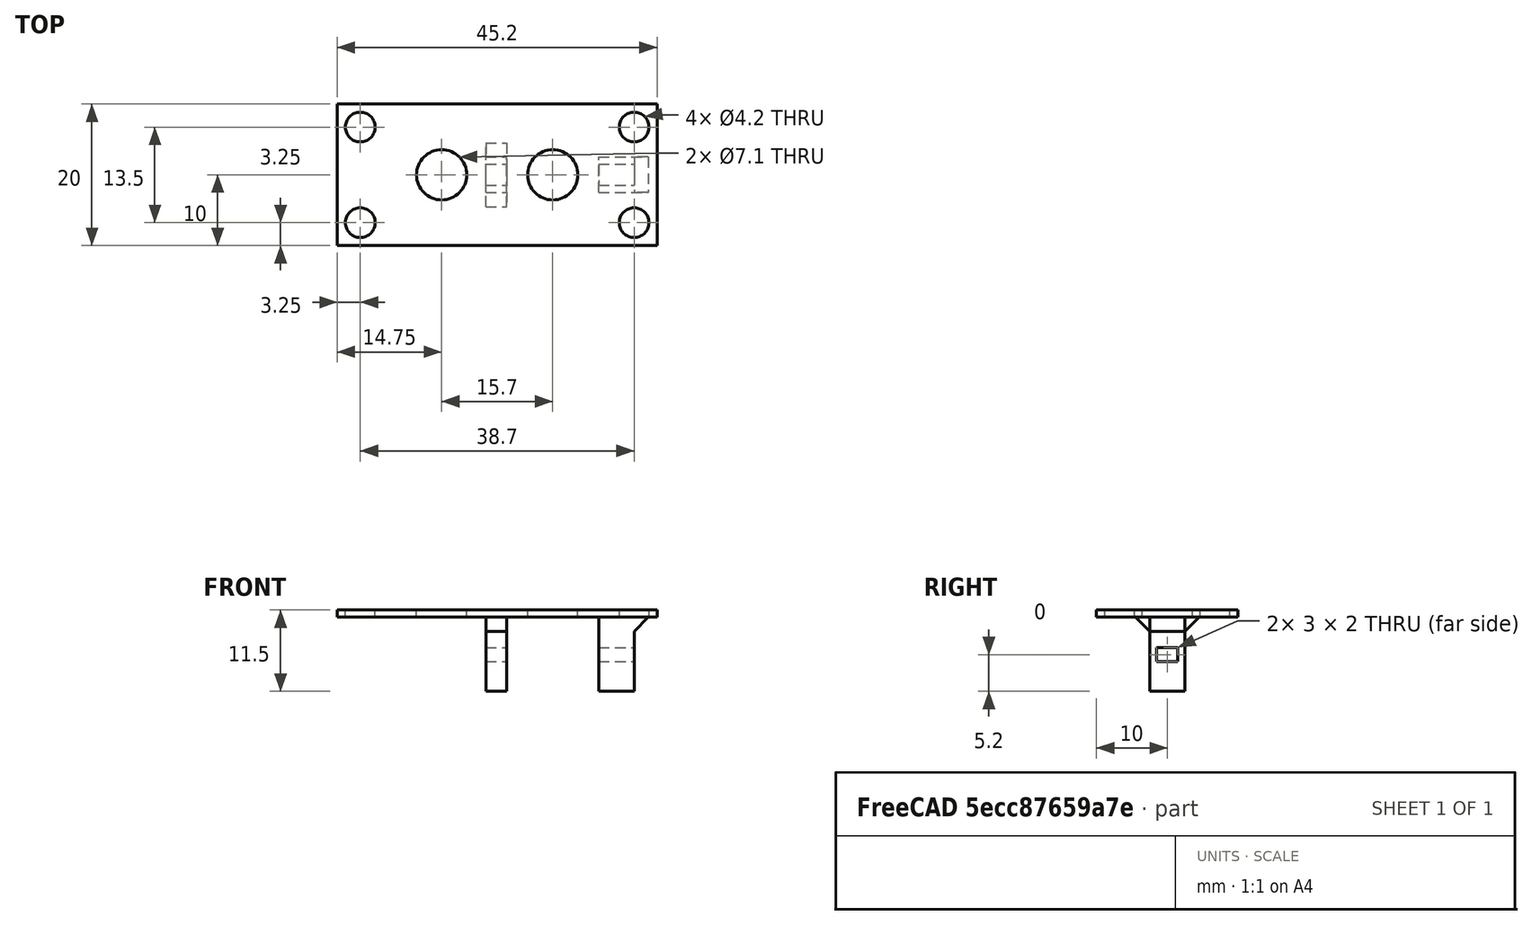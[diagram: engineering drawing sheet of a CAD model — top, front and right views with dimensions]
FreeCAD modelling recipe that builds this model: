
FCSTD DOCUMENT  (FreeCAD 0.17R13522 (Git))
Label: v5_base2_media_con_soportes
License: CreativeCommons Attribution-ShareAlike
LicenseURL: http://creativecommons.org/licenses/by-sa/4.0/
objects: Part::Cut×17, Part::Box×10, Part::Cylinder×8, Part::Feature×6, Part::Fuse×6, Part::Chamfer×4
note: 51 computed .brp shape members not serialized (recipe doc carries the construction recipe); baked Part::Feature solids carry a one-line shape summary decoded from their .brp

FEATURE [Part::Box] Box  label="base"
  AttacherType = Attacher::AttachEngine3D
  Height = 2
  Length = 45.2
  Width = 20
FEATURE [Part::Cylinder] Cylinder  label="cortador izquierda"
  Angle = 360
  AttacherType = Attacher::AttachEngine3D
  Height = 60
  Placement = pos=(14.75,10,-12) rot=(0,0,1;0rad)
  Radius = 3.55
FEATURE [Part::Feature] Cylinder001  label="cortador derecha"
  Placement = pos=(30.45,10,-4) rot=(0,0,1;0rad)
  shape: bbox 7.1 x 7.1 x 10 mm, 3 faces (baked)
FEATURE [Part::Cylinder] Cylinder002  label="sacabocado_abajo_izq"
  Angle = 360
  AttacherType = Attacher::AttachEngine3D
  Height = 10
  Placement = pos=(3,3,-4) rot=(0,0,1;0rad)
  Radius = 1.75
FEATURE [Part::Feature] Cylinder002001  label="sacabocado_abajo_derecha"
  Placement = pos=(42.2,3,-4) rot=(0,0,1;0rad)
  shape: bbox 3.5 x 3.5 x 10 mm, 3 faces (baked)
FEATURE [Part::Feature] Cylinder002002  label="sacabocado_arriba_izq"
  Placement = pos=(3,17,-4) rot=(0,0,1;0rad)
  shape: bbox 3.5 x 3.5 x 10 mm, 3 faces (baked)
FEATURE [Part::Feature] Cylinder002002001  label="sacabocado_arriba_derecha"
  Placement = pos=(42.2,17,-4) rot=(0,0,1;0rad)
  shape: bbox 3.5 x 3.5 x 10 mm, 3 faces (baked)
FEATURE [Part::Cylinder] Cylinder002002002  label="cilindro interior"
  Angle = 360
  AttacherType = Attacher::AttachEngine3D
  Height = 38.5
  Placement = pos=(14.75,10,0) rot=(0,0,1;0rad)
  Radius = 4.5
FEATURE [Part::Cylinder] Cylinder002002003  label="base cilindrica grande"
  Angle = 360
  AttacherType = Attacher::AttachEngine3D
  Height = 8.5
  Placement = pos=(14.75,10,0) rot=(0,0,1;0rad)
  Radius = 7
FEATURE [Part::Cut] Cut
  Base = -> Box
  Refine = true
  Tool = -> Cylinder002
FEATURE [Part::Cut] Cut001
  Base = -> Cut
  Refine = true
  Tool = -> Cylinder002001
FEATURE [Part::Cut] Cut002
  Base = -> Cut001
  Refine = true
  Tool = -> Cylinder001
FEATURE [Part::Cut] Cut003
  Base = -> Cut002
  Refine = true
  Tool = -> Cylinder002002001
FEATURE [Part::Cut] Cut004
  Base = -> Cut003
  Refine = true
  Tool = -> Cylinder002002
FEATURE [Part::Fuse] Fusion
  Base = -> Cylinder002002003
  Refine = true
  Tool = -> Cut004
FEATURE [Part::Fuse] Fusion001
  Base = -> Cylinder002002002
  Refine = true
  Tool = -> Fusion
FEATURE [Part::Cut] Cut005  label="pieza sin soportes"
  Base = -> Fusion001
  Refine = true
  Tool = -> Cylinder
FEATURE [Part::Box] Box001  label="soporte1"
  AttacherType = Attacher::AttachEngine3D
  Height = 10.5
  Length = 5
  Placement = pos=(36.95,7.5,-10.5) rot=(0,0,1;0rad)
  Width = 5
FEATURE [Part::Feature] Box001001  label="soporte2"
  Placement = pos=(18.95,7.5,-10.5) rot=(0,0,1;0rad)
  shape: bbox 5 x 5 x 10.5 mm, 6 faces (baked)
FEATURE [Part::Box] Box001002  label="perforador chavetas"
  AttacherType = Attacher::AttachEngine3D
  Height = 2
  Length = 30
  Placement = pos=(16,8.5,-6.3) rot=(0,0,1;0rad)
  Width = 3
FEATURE [Part::Feature] Box001002001  label="perforador chavetas001"
  Placement = pos=(16,8.5,-6.3) rot=(0,0,1;0rad)
  shape: bbox 30 x 3 x 2 mm, 6 faces (baked)
FEATURE [Part::Cut] Cut006
  Base = -> Box001
  Refine = true
  Tool = -> Box001002
FEATURE [Part::Cut] Cut007
  Base = -> Box001001
  Refine = true
  Tool = -> Box001002001
FEATURE [Part::Fuse] Fusion002
  Base = -> Cut005
  Refine = true
  Tool = -> Cut007
FEATURE [Part::Fuse] Fusion003
  Base = -> Cut006
  Refine = true
  Tool = -> Fusion002
FEATURE [Part::Chamfer] Chamfer
  Base = -> Fusion003
  Edges = 1 edges r=2: [Edge29]
FEATURE [Part::Chamfer] Chamfer001
  Base = -> Chamfer
  Edges = 1 edges r=2: [Edge19]
FEATURE [Part::Chamfer] Chamfer002  label="pieza completa"
  Base = -> Chamfer001
  Edges = 2 edges r=2: [Edge4,Edge10]
FEATURE [Part::Box] Box001002002  label="cortador separa pieza 2"
  AttacherType = Attacher::AttachEngine3D
  Height = 26
  Length = 58
  Placement = pos=(-10.65,-6,1) rot=(0,0,1;0rad)
  Width = 30
FEATURE [Part::Box] Box001002004  label="Cube"
  AttacherType = Attacher::AttachEngine3D
  Height = 30
  Length = 30
  Placement = pos=(0,0,18) rot=(0,0,1;0rad)
  Width = 30
FEATURE [Part::Cut] Cut008
  Base = -> Chamfer002
  Refine = true
  Tool = -> Box001002004
FEATURE [Part::Cut] Cut009
  Base = -> Cut008
  Refine = true
  Tool = -> Box001002002
FEATURE [Part::Cylinder] Cylinder002002004  label="Cylinder"
  Angle = 360
  AttacherType = Attacher::AttachEngine3D
  Height = 10
  Placement = pos=(41.95,16.75,-4) rot=(0,0,1;0rad)
  Radius = 2.1
FEATURE [Part::Cylinder] Cylinder002002005  label="Cylinder001"
  Angle = 360
  AttacherType = Attacher::AttachEngine3D
  Height = 10
  Placement = pos=(41.95,3.25,-3.5) rot=(0,0,1;0rad)
  Radius = 2.1
FEATURE [Part::Cylinder] Cylinder002002006  label="Cylinder002"
  Angle = 360
  AttacherType = Attacher::AttachEngine3D
  Height = 10
  Placement = pos=(3.25,16.75,-4) rot=(0,0,1;0rad)
  Radius = 2.1
FEATURE [Part::Cylinder] Cylinder002002007  label="Cylinder003"
  Angle = 360
  AttacherType = Attacher::AttachEngine3D
  Height = 10
  Placement = pos=(3.25,3.25,-4) rot=(0,0,1;0rad)
  Radius = 2.1
FEATURE [Part::Box] Box001002005  label="Cube001"
  AttacherType = Attacher::AttachEngine3D
  Height = 1
  Length = 10
  Width = 20
FEATURE [Part::Fuse] Fusion004
  Base = -> Cut009
  Refine = true
  Tool = -> Box001002005
FEATURE [Part::Cut] Cut010
  Base = -> Fusion004
  Refine = true
  Tool = -> Cylinder002002007
FEATURE [Part::Cut] Cut011
  Base = -> Cut010
  Refine = true
  Tool = -> Cylinder002002006
FEATURE [Part::Box] Box001002006  label="Cube002"
  AttacherType = Attacher::AttachEngine3D
  Height = 1
  Length = 10
  Placement = pos=(35,0,0) rot=(0,0,1;0rad)
  Width = 20
FEATURE [Part::Fuse] Fusion005
  Base = -> Cut011
  Refine = true
  Tool = -> Box001002006
FEATURE [Part::Cut] Cut012
  Base = -> Fusion005
  Refine = true
  Tool = -> Cylinder002002004
FEATURE [Part::Cut] Cut013
  Base = -> Cut012
  Refine = true
  Tool = -> Cylinder002002005
FEATURE [Part::Box] Box001002007  label="Cube003"
  AttacherType = Attacher::AttachEngine3D
  Height = 6
  Length = 6
  Placement = pos=(36,12.5,-6) rot=(0,0,1;0rad)
  Width = 2
FEATURE [Part::Cut] Cut014
  Base = -> Cut013
  Refine = true
  Tool = -> Box001002007
FEATURE [Part::Box] Box001002008  label="Cube004"
  AttacherType = Attacher::AttachEngine3D
  Height = 10
  Length = 6
  Placement = pos=(36.5,5.5,-10) rot=(0,0,1;0rad)
  Width = 2
FEATURE [Part::Cut] Cut015
  Base = -> Cut014
  Refine = true
  Tool = -> Box001002008
FEATURE [Part::Chamfer] Chamfer003
  Base = -> Cut015
  Edges = 1 edges r=2: [Edge38]
FEATURE [Part::Box] Box001002009  label="Cube005"
  AttacherType = Attacher::AttachEngine3D
  Height = 18
  Length = 10
  Placement = pos=(11,0,-18) rot=(0,0,1;0rad)
  Width = 20
FEATURE [Part::Cut] Cut016
  Base = -> Chamfer003
  Refine = true
  Tool = -> Box001002009
